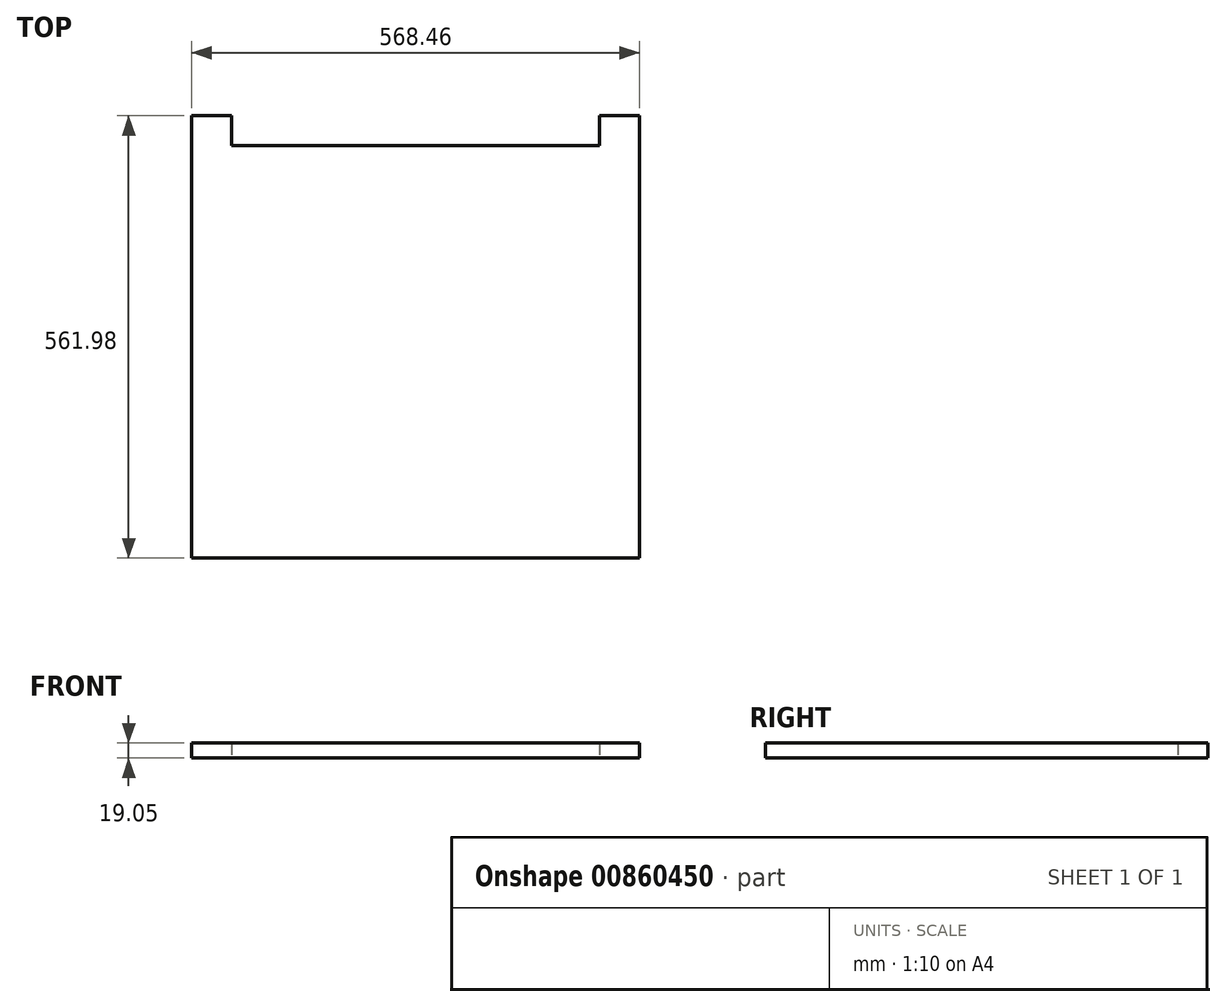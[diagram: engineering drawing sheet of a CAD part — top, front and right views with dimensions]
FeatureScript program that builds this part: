
annotation { "Feature Type Name" : "Feature", "Feature Type Description" : "" }
export const myFeature = defineFeature(function(context is Context, id is Id, definition is map)
    precondition{}
    {
        {
            var Q0;
            Q0=qCreatedBy(makeId("Top.planeOp"),FACE);
            var sketch = newSketch(context, id + "F0", { "sketchPlane" : qUnion([Q0])});
            skLineSegment(sketch, "E0.bottom", {"start": v(284.23, 280.99) * mm, "end": v(-284.23, 280.99) * mm});
            skLineSegment(sketch, "E0.top", {"start": v(284.23, -280.99) * mm, "end": v(-284.23, -280.99) * mm});
            skLineSegment(sketch, "E0.left", {"start": v(284.23, 280.99) * mm, "end": v(284.23, -280.99) * mm});
            skLineSegment(sketch, "E0.right", {"start": v(-284.23, 280.99) * mm, "end": v(-284.23, -280.99) * mm});
            skPoint(sketch, "E0.middle", {"position": v(0, 0) * mm});
            skLineSegment(sketch, "E1", {"start": v(-284.23, 280.99) * mm, "end": v(-233.43, 280.99) * mm});
            skLineSegment(sketch, "E2", {"start": v(284.23, 280.99) * mm, "end": v(233.43, 280.99) * mm});
            skLineSegment(sketch, "E3", {"start": v(-233.43, 280.99) * mm, "end": v(-233.43, 242.89) * mm});
            skLineSegment(sketch, "E4", {"start": v(-233.43, 242.89) * mm, "end": v(233.43, 242.89) * mm});
            skLineSegment(sketch, "E5", {"start": v(233.43, 242.89) * mm, "end": v(233.43, 280.99) * mm});
            skSolve(sketch);
        }
        {
            var Q0;
            Q0=makeQuery(id+"F0.imprint","IMPRINT",FACE,{"disambiguationData":[TD([[makeQuery(id+"F0.imprint","IMPRINT",EDGE,{"derivedFrom":sQuery(id+"F0.wireOp",EDGE,"E0.top")}),-1.0]])]});
            extrude(context, id + "F1", {"entities" : qUnion([Q0]), "depth" : 19.05 * mm, "offsetDistance" : 25.4 * mm});
        }
    });
